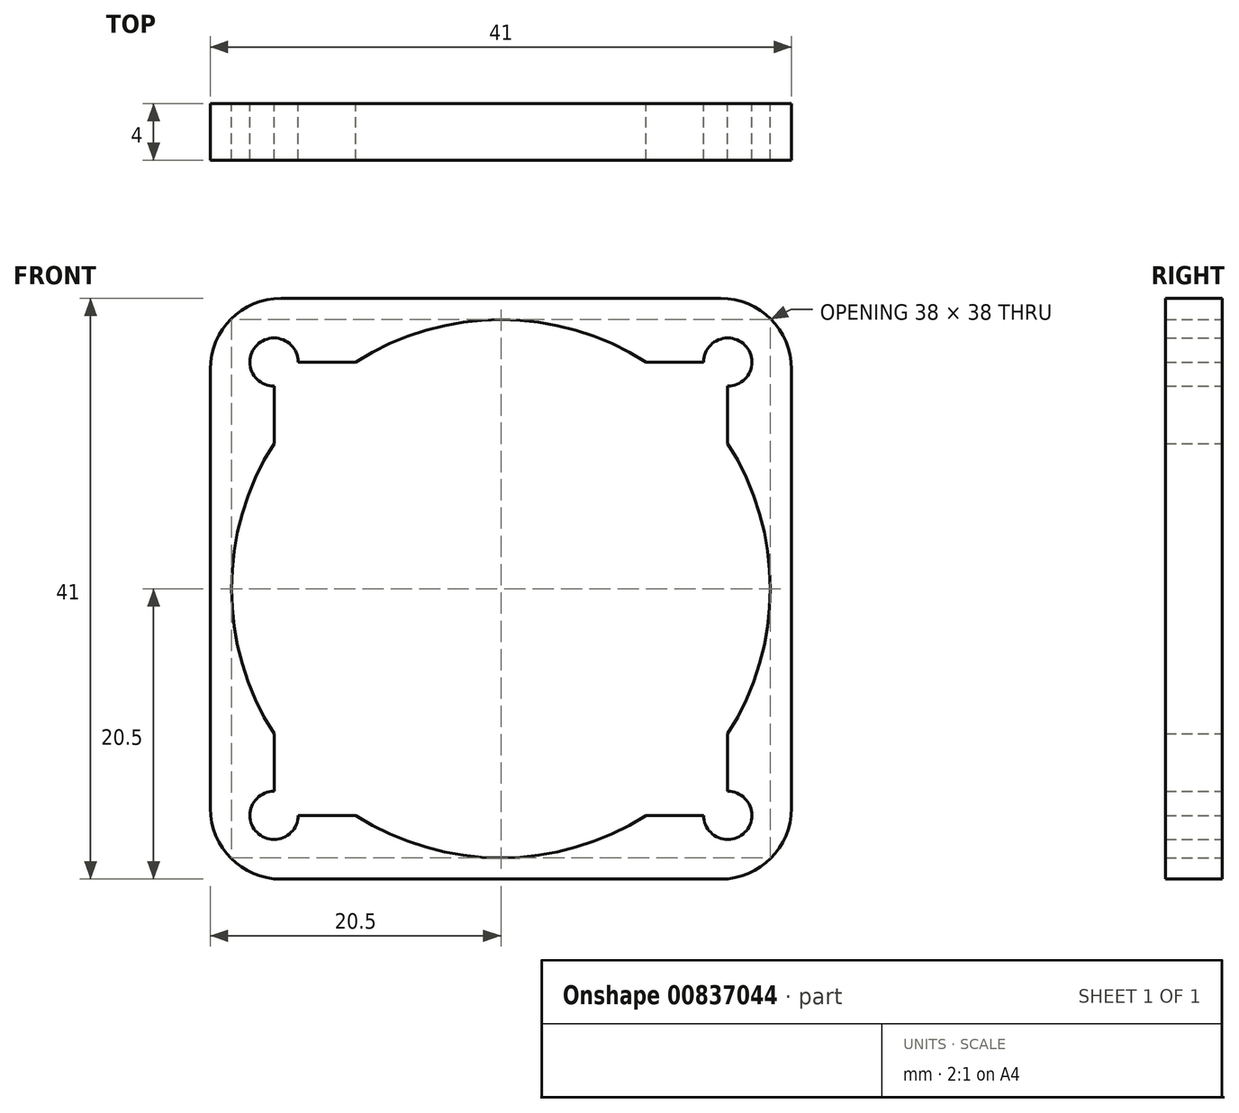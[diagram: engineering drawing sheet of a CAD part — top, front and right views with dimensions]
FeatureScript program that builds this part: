
annotation { "Feature Type Name" : "Feature", "Feature Type Description" : "" }
export const myFeature = defineFeature(function(context is Context, id is Id, definition is map)
    precondition{}
    {
        {
            var Q0;
            Q0=qCreatedBy(makeId("Front.planeOp"),FACE);
            var sketch = newSketch(context, id + "F0", { "sketchPlane" : qUnion([Q0])});
            skLineSegment(sketch, "E0.bottom", {"start": v(16, 16) * mm, "end": v(-16, 16) * mm});
            skLineSegment(sketch, "E0.top", {"start": v(16, -16) * mm, "end": v(-16, -16) * mm});
            skLineSegment(sketch, "E0.left", {"start": v(16, 16) * mm, "end": v(16, -16) * mm});
            skLineSegment(sketch, "E0.right", {"start": v(-16, 16) * mm, "end": v(-16, -16) * mm});
            skPoint(sketch, "E0.middle", {"position": v(0, 0) * mm});
            skLineSegment(sketch, "E1.bottom", {"start": v(20.5, 20.5) * mm, "end": v(-20.5, 20.5) * mm});
            skLineSegment(sketch, "E1.top", {"start": v(20.5, -20.5) * mm, "end": v(-20.5, -20.5) * mm});
            skLineSegment(sketch, "E1.left", {"start": v(20.5, 20.5) * mm, "end": v(20.5, -20.5) * mm});
            skLineSegment(sketch, "E1.right", {"start": v(-20.5, 20.5) * mm, "end": v(-20.5, -20.5) * mm});
            skCircle(sketch, "E2", {"center": v(-16, 16) * mm, "radius": 1.7 * mm});
            skCircle(sketch, "E3", {"center": v(16, 16) * mm, "radius": 1.7 * mm});
            skCircle(sketch, "E4", {"center": v(16, -16) * mm, "radius": 1.7 * mm});
            skCircle(sketch, "E5", {"center": v(-16, -16) * mm, "radius": 1.7 * mm});
            skCircle(sketch, "E6", {"center": v(0, 0) * mm, "radius": 19 * mm});
            skSolve(sketch);
        }
        {
            var Q0;
            {var subQ3=sQuery(id+"F0.wireOp",EDGE,"E1.bottom");Q0=makeQuery(id+"F0.imprint","IMPRINT",FACE,{"disambiguationData":[TD([[makeQuery(id+"F0.imprint","IMPRINT",EDGE,{"derivedFrom":subQ3}),1.0]])]});}
            extrude(context, id + "F1", {"entities" : qUnion([Q0]), "depth" : 4 * mm, "offsetDistance" : 25 * mm});
        }
        {
            var Q0;
            Q0=makeQuery(id+"F1.opExtrude","SWEPT_EDGE",EDGE,{"disambiguationData":[OSD([sQuery(id+"F0.wireOp",EDGE,"E1.top"),sQuery(id+"F0.wireOp",EDGE,"E1.right")])]});
            var Q1;
            Q1=makeQuery(id+"F1.opExtrude","SWEPT_EDGE",EDGE,{"disambiguationData":[OSD([sQuery(id+"F0.wireOp",EDGE,"E1.top"),sQuery(id+"F0.wireOp",EDGE,"E1.left")])]});
            var Q2;
            Q2=makeQuery(id+"F1.opExtrude","SWEPT_EDGE",EDGE,{"disambiguationData":[OSD([sQuery(id+"F0.wireOp",EDGE,"E1.bottom"),sQuery(id+"F0.wireOp",EDGE,"E1.left")])]});
            var Q3;
            Q3=makeQuery(id+"F1.opExtrude","SWEPT_EDGE",EDGE,{"disambiguationData":[OSD([sQuery(id+"F0.wireOp",EDGE,"E1.bottom"),sQuery(id+"F0.wireOp",EDGE,"E1.right")])]});
            fillet(context, id + "F2", {"entities" : qUnion([Q0, Q1, Q2, Q3]), "radius" : 5 * mm, "tangentPropagation" : true, "allowEdgeOverflow" : false});
        }
    });
